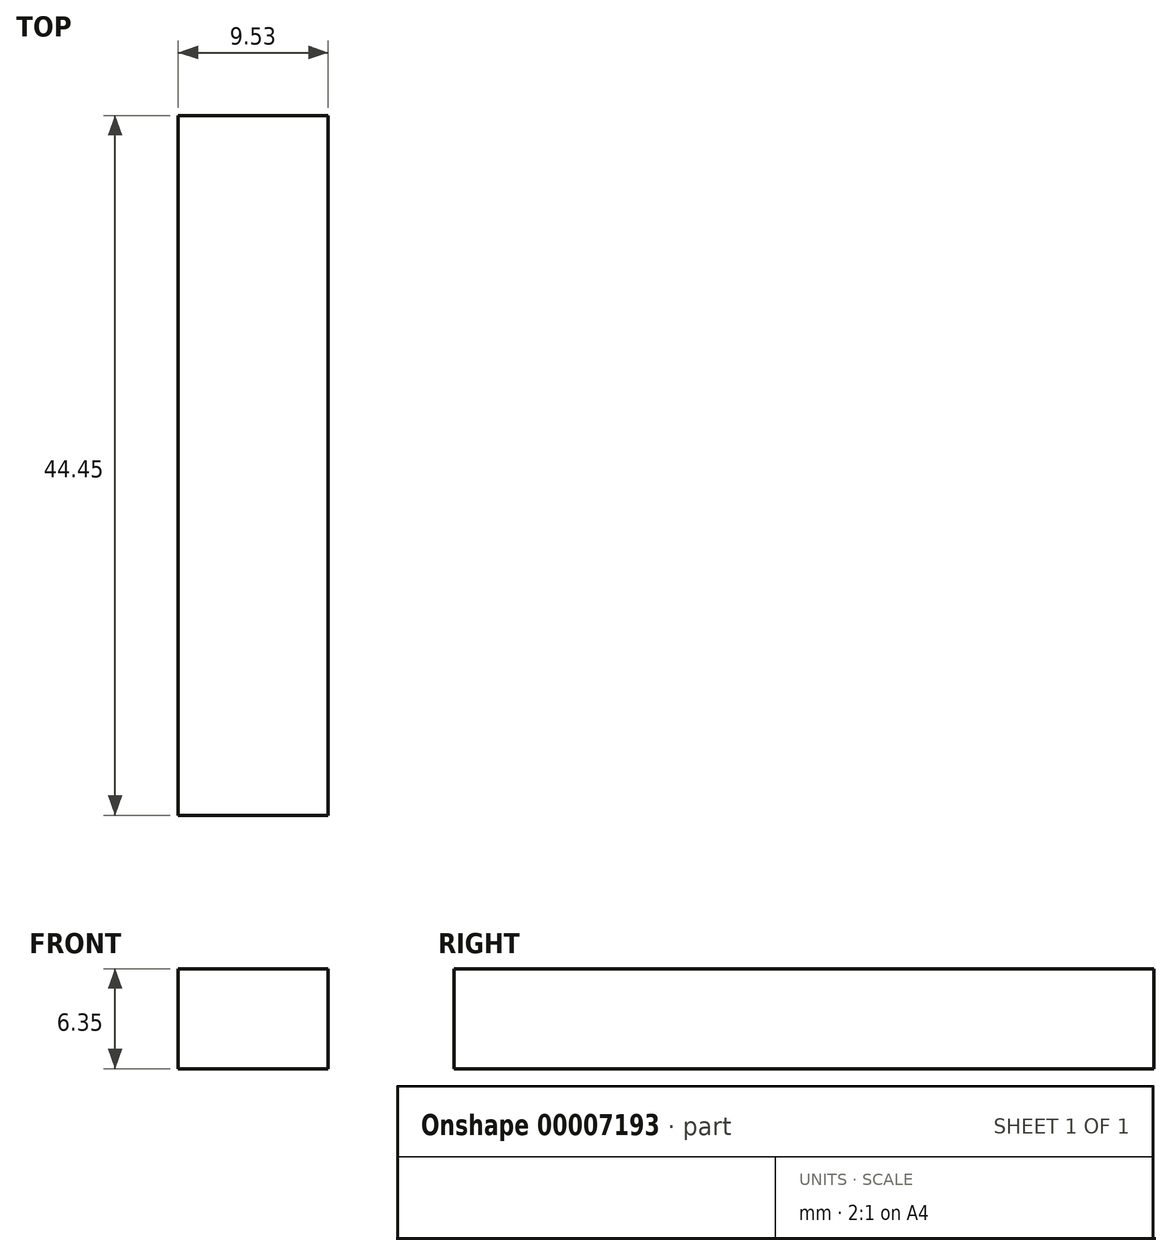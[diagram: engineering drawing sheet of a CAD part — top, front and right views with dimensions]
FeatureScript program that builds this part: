
annotation { "Feature Type Name" : "Feature", "Feature Type Description" : "" }
export const myFeature = defineFeature(function(context is Context, id is Id, definition is map)
    precondition{}
    {
        {
            var Q0;
            Q0=qCreatedBy(makeId("Right.planeOp"),FACE);
            var sketch = newSketch(context, id + "F0", { "sketchPlane" : qUnion([Q0])});
            skLineSegment(sketch, "E0.bottom", {"start": v(31.82, 4.92) * mm, "end": v(-12.63, 4.92) * mm});
            skLineSegment(sketch, "E0.top", {"start": v(31.82, -1.43) * mm, "end": v(-12.63, -1.43) * mm});
            skLineSegment(sketch, "E0.left", {"start": v(31.82, 4.92) * mm, "end": v(31.82, -1.43) * mm});
            skLineSegment(sketch, "E0.right", {"start": v(-12.63, 4.92) * mm, "end": v(-12.63, -1.43) * mm});
            skSolve(sketch);
        }
        {
            var Q0;
            Q0=makeQuery(id+"F0.imprint","IMPRINT",FACE,{"disambiguationData":[TD([[makeQuery(id+"F0.imprint","IMPRINT",EDGE,{"derivedFrom":sQuery(id+"F0.wireOp",EDGE,"E0.bottom")}),1.0]])]});
            extrude(context, id + "F1", {"entities" : qUnion([Q0]), "depth" : 9.52 * mm});
        }
    });
